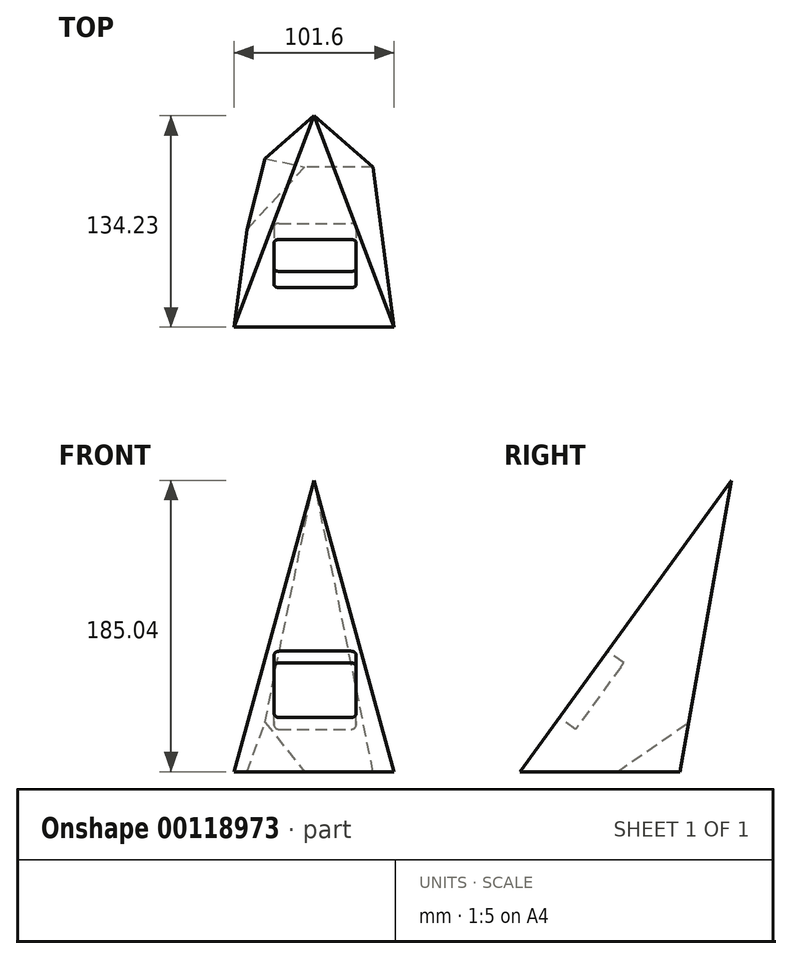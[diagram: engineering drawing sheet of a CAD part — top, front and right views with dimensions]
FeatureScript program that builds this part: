
annotation { "Feature Type Name" : "Feature", "Feature Type Description" : "" }
export const myFeature = defineFeature(function(context is Context, id is Id, definition is map)
    precondition{}
    {
        {
            var Q0;
            Q0=qCreatedBy(makeId("Right.planeOp"),FACE);
            var sketch = newSketch(context, id + "F0", { "sketchPlane" : qUnion([Q0])});
            skLineSegment(sketch, "E0", {"start": v(-38.9, 0) * mm, "end": v(62.7, 0) * mm});
            skLineSegment(sketch, "E1", {"start": v(-38.9, 0) * mm, "end": v(95.33, 185.04) * mm});
            skLineSegment(sketch, "E2", {"start": v(62.7, 0) * mm, "end": v(95.33, 185.04) * mm});
            skSolve(sketch);
        }
        {
            var Q0;
            Q0=makeQuery(id+"F0.imprint","IMPRINT",FACE,{"disambiguationData":[TD([[makeQuery(id+"F0.imprint","IMPRINT",EDGE,{"derivedFrom":sQuery(id+"F0.wireOp",EDGE,"E0")}),1.0]])]});
            extrude(context, id + "F1", {"entities" : qUnion([Q0]), "depth" : 101.6 * mm});
        }
        {
            var Q0;
            Q0=makeQuery(id+"F1.opExtrude","SWEPT_FACE",FACE,{"disambiguationData":[OSD([sQuery(id+"F0.wireOp",EDGE,"E1")])]});
            var sketch = newSketch(context, id + "F2", { "sketchPlane" : qUnion([Q0])});
            skLineSegment(sketch, "E3", {"start": v(0, -22.84) * mm, "end": v(50.8, 205.76) * mm});
            skLineSegment(sketch, "E4", {"start": v(101.6, -22.84) * mm, "end": v(50.8, 205.76) * mm});
            skLineSegment(sketch, "E5", {"start": v(0, 205.76) * mm, "end": v(0, -22.84) * mm});
            skLineSegment(sketch, "E6", {"start": v(0, 205.76) * mm, "end": v(50.8, 205.76) * mm});
            skLineSegment(sketch, "E7", {"start": v(50.8, 205.76) * mm, "end": v(101.6, 205.76) * mm});
            skLineSegment(sketch, "E8", {"start": v(101.6, 205.76) * mm, "end": v(101.6, -22.84) * mm});
            skSolve(sketch);
        }
        {
            var Q0;
            Q0 = qSketchRegion(id + "F2", true);
            extrude(context, id + "F3", {"entities" : qUnion([Q0]), "operationType" : NewBodyOperationType.REMOVE, "endBound" : BoundingType.THROUGH_ALL, "oppositeDirection" : true, "depth" : 25.4 * mm});
        }
        {
            var Q0;
            Q0=makeQuery(id+"F1.opExtrude","SWEPT_FACE",FACE,{"disambiguationData":[OSD([sQuery(id+"F0.wireOp",EDGE,"E1")])]});
            var sketch = newSketch(context, id + "F4", { "sketchPlane" : qUnion([Q0])});
            skLineSegment(sketch, "E9.bottom", {"start": v(25.45, 71.84) * mm, "end": v(77.52, 71.84) * mm});
            skLineSegment(sketch, "E9.top", {"start": v(25.45, 19.77) * mm, "end": v(77.52, 19.77) * mm});
            skLineSegment(sketch, "E9.left", {"start": v(25.45, 71.84) * mm, "end": v(25.45, 19.77) * mm});
            skLineSegment(sketch, "E9.right", {"start": v(77.52, 71.84) * mm, "end": v(77.52, 19.77) * mm});
            skLineSegment(sketch, "E10", {"start": v(50.8, -22.84) * mm, "end": v(50.8, 205.76) * mm, "construction": true});
            skLineSegment(sketch, "E11", {"start": v(25.45, 71.84) * mm, "end": v(77.52, 19.77) * mm, "construction": true});
            skLineSegment(sketch, "E12", {"start": v(25.45, 19.77) * mm, "end": v(77.52, 71.84) * mm, "construction": true});
            skSolve(sketch);
        }
        {
            var Q0;
            Q0 = qSketchRegion(id + "F4", true);
            extrude(context, id + "F5", {"entities" : qUnion([Q0]), "operationType" : NewBodyOperationType.REMOVE, "oppositeDirection" : true, "depth" : 12.7 * mm});
        }
        {
            var Q0;
            Q0=makeQuery(id+"F5.boolean.opBoolean","COPY",EDGE,{"derivedFrom":makeQuery(id+"F5.opExtrude","SWEPT_EDGE",EDGE,{"disambiguationData":[OSD([sQuery(id+"F4.wireOp",EDGE,"E9.bottom"),sQuery(id+"F4.wireOp",EDGE,"E9.left")])]})});
            fillet(context, id + "F6", {"entities" : qUnion([Q0]), "radius" : 3.17 * mm, "tangentPropagation" : true, "allowEdgeOverflow" : false});
        }
        {
            var Q0;
            Q0=makeQuery(id+"F5.boolean.opBoolean","COPY",EDGE,{"derivedFrom":makeQuery(id+"F5.opExtrude","SWEPT_EDGE",EDGE,{"disambiguationData":[OSD([sQuery(id+"F4.wireOp",EDGE,"E9.top"),sQuery(id+"F4.wireOp",EDGE,"E9.left")])]})});
            var Q1;
            Q1=makeQuery(id+"F5.boolean.opBoolean","COPY",EDGE,{"derivedFrom":makeQuery(id+"F5.opExtrude","SWEPT_EDGE",EDGE,{"disambiguationData":[OSD([sQuery(id+"F4.wireOp",EDGE,"E9.top"),sQuery(id+"F4.wireOp",EDGE,"E9.right")])]})});
            var Q2;
            Q2=makeQuery(id+"F5.boolean.opBoolean","COPY",EDGE,{"derivedFrom":makeQuery(id+"F5.opExtrude","SWEPT_EDGE",EDGE,{"disambiguationData":[OSD([sQuery(id+"F4.wireOp",EDGE,"E9.bottom"),sQuery(id+"F4.wireOp",EDGE,"E9.right")])]})});
            fillet(context, id + "F7", {"entities" : qUnion([Q0, Q1, Q2]), "radius" : 3.17 * mm, "tangentPropagation" : true, "allowEdgeOverflow" : false});
        }
        {
            var Q0;
            Q0=makeQuery(id+"F1.opExtrude","SWEPT_FACE",FACE,{"disambiguationData":[OSD([sQuery(id+"F0.wireOp",EDGE,"E0")])]});
            var sketch = newSketch(context, id + "F8", { "sketchPlane" : qUnion([Q0])});
            skLineSegment(sketch, "E13", {"start": v(44.78, -62.7) * mm, "end": v(8.06, -22.88) * mm});
            skLineSegment(sketch, "E14", {"start": v(44.78, -62.7) * mm, "end": v(13.26, -62.7) * mm});
            skLineSegment(sketch, "E15", {"start": v(13.26, -62.7) * mm, "end": v(8.06, -22.88) * mm});
            skSolve(sketch);
        }
        {
            var Q0;
            Q0=sQuery(id+"F8.wireOp",EDGE,"E13");
            var Q1;
            Q1=makeQuery(id+"F3.boolean.opBoolean","INTERSECT",EDGE,{"derivedFrom":[makeQuery(id+"F1.opExtrude","SWEPT_FACE",FACE,{"disambiguationData":[OSD([sQuery(id+"F0.wireOp",EDGE,"E2")])]}),makeQuery(id+"F3.opExtrude","SWEPT_FACE",FACE,{"disambiguationData":[OSD([sQuery(id+"F2.wireOp",EDGE,"E3")])]})]});
            cPlane(context, id + "F9", {"entities" : qUnion([Q0, Q1]), "cplaneType" : CPlaneType.LINE_ANGLE, "offset" : 25.4 * mm, "angle" : 37 * degree, "width" : 152.4 * mm, "height" : 152.4 * mm});
        }
        {
            var Q0;
            Q0=qCreatedBy(id+"F9.planeOp",FACE);
            var sketch = newSketch(context, id + "F10", { "sketchPlane" : qUnion([Q0])});
            skLineSegment(sketch, "E16.bottom", {"start": v(-3.18, 30.36) * mm, "end": v(-117.4, 30.36) * mm});
            skLineSegment(sketch, "E16.top", {"start": v(-3.18, -73.53) * mm, "end": v(-117.4, -73.53) * mm});
            skLineSegment(sketch, "E16.left", {"start": v(-3.18, 30.36) * mm, "end": v(-3.18, -73.53) * mm});
            skLineSegment(sketch, "E16.right", {"start": v(-117.4, 30.36) * mm, "end": v(-117.4, -73.53) * mm});
            skSolve(sketch);
        }
        {
            var Q0;
            Q0=makeQuery(id+"F10.imprint","IMPRINT",FACE,{"disambiguationData":[TD([[makeQuery(id+"F10.imprint","IMPRINT",EDGE,{"derivedFrom":sQuery(id+"F10.wireOp",EDGE,"E16.bottom")}),1.0]])]});
            extrude(context, id + "F11", {"entities" : qUnion([Q0]), "operationType" : NewBodyOperationType.REMOVE, "depth" : 25.4 * mm});
        }
    });
